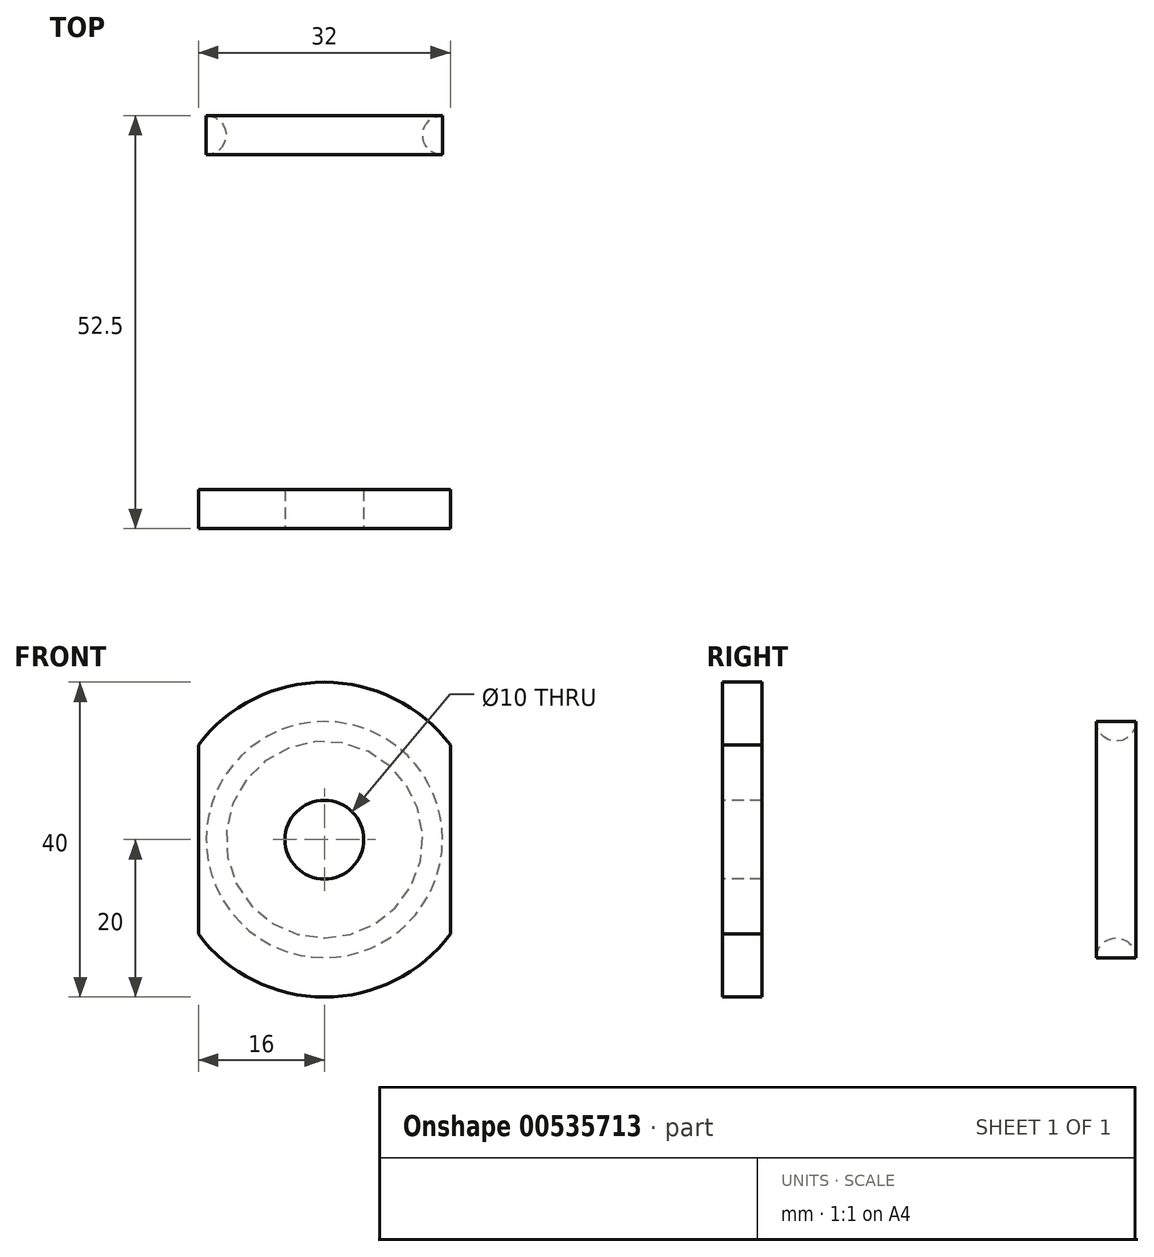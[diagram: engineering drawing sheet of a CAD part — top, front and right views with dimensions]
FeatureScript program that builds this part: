
annotation { "Feature Type Name" : "Feature", "Feature Type Description" : "" }
export const myFeature = defineFeature(function(context is Context, id is Id, definition is map)
    precondition{}
    {
        {
            var Q0;
            Q0=qCreatedBy(makeId("Front.planeOp"),FACE);
            var sketch = newSketch(context, id + "F0", { "sketchPlane" : qUnion([Q0])});
            skCircle(sketch, "E0", {"center": v(0, 0) * mm, "radius": 20 * mm});
            skLineSegment(sketch, "E1", {"start": v(0, 0) * mm, "end": v(16, 0) * mm});
            skLineSegment(sketch, "E2", {"start": v(16, 0) * mm, "end": v(16, 12) * mm});
            skLineSegment(sketch, "E3", {"start": v(16, 12) * mm, "end": v(16, -12) * mm});
            skLineSegment(sketch, "E4", {"start": v(0, 0) * mm, "end": v(-16, 0) * mm});
            skLineSegment(sketch, "E5", {"start": v(-16, 0) * mm, "end": v(-16, 12) * mm});
            skLineSegment(sketch, "E6", {"start": v(-16, 12) * mm, "end": v(-16, -12) * mm});
            skSolve(sketch);
        }
        {
            var Q0;
            {var subQ1=sQuery(id+"F0.wireOp",EDGE,"E1");Q0=makeQuery(id+"F0.imprint","IMPRINT",FACE,{"disambiguationData":[TD([[makeQuery(id+"F0.imprint","IMPRINT",EDGE,{"derivedFrom":subQ1}),1.0]])]});}
            var Q1;
            {var subQ1=sQuery(id+"F0.wireOp",EDGE,"E1");Q1=makeQuery(id+"F0.imprint","IMPRINT",FACE,{"disambiguationData":[TD([[makeQuery(id+"F0.imprint","IMPRINT",EDGE,{"derivedFrom":subQ1}),-1.0]])]});}
            extrude(context, id + "F1", {"entities" : qUnion([Q0, Q1]), "depth" : 5 * mm, "offsetDistance" : 25 * mm});
        }
        {
            var Q0;
            {var subQ1=sQuery(id+"F0.wireOp",EDGE,"E1");Q0=makeQuery(id+"F0.imprint","IMPRINT",FACE,{"disambiguationData":[TD([[makeQuery(id+"F0.imprint","IMPRINT",EDGE,{"derivedFrom":subQ1}),1.0]])]});}
            var sketch = newSketch(context, id + "F2", { "sketchPlane" : qUnion([Q0])});
            skCircle(sketch, "E7", {"center": v(0, 0) * mm, "radius": 15 * mm});
            skSolve(sketch);
        }
        {
            var Q0;
            Q0=qSketchRegion(id+"F2",true);
            extrude(context, id + "F3", {"entities" : qUnion([Q0]), "operationType" : NewBodyOperationType.ADD, "oppositeDirection" : true, "depth" : 55 * mm, "offsetDistance" : 25 * mm});
        }
        {
            var Q0;
            Q0=qCreatedBy(makeId("Front.planeOp"),FACE);
            var sketch = newSketch(context, id + "F4", { "sketchPlane" : qUnion([Q0])});
            skCircle(sketch, "E8", {"center": v(0, 0) * mm, "radius": 5 * mm});
            skSolve(sketch);
        }
        {
            var Q0;
            Q0=qSketchRegion(id+"F4",true);
            extrude(context, id + "F5", {"entities" : qUnion([Q0]), "operationType" : NewBodyOperationType.REMOVE, "endBound" : BoundingType.UP_TO_NEXT, "oppositeDirection" : true, "depth" : 25 * mm, "offsetDistance" : 25 * mm});
        }
        {
            var Q0;
            Q0=qSketchRegion(id+"F4",true);
            extrude(context, id + "F6", {"entities" : qUnion([Q0]), "operationType" : NewBodyOperationType.REMOVE, "endBound" : BoundingType.UP_TO_NEXT, "depth" : 25 * mm, "offsetDistance" : 25 * mm});
        }
        {
            var Q0;
            Q0=qCreatedBy(makeId("Right.planeOp"),FACE);
            var sketch = newSketch(context, id + "F7", { "sketchPlane" : qUnion([Q0])});
            skLineSegment(sketch, "E9.bottom", {"start": v(0, 0) * mm, "end": v(55, 0) * mm});
            skLineSegment(sketch, "E9.top", {"start": v(0, 15) * mm, "end": v(55, 15) * mm});
            skLineSegment(sketch, "E9.left", {"start": v(0, 0) * mm, "end": v(0, 15) * mm});
            skLineSegment(sketch, "E9.right", {"start": v(55, 0) * mm, "end": v(55, 15) * mm});
            skLineSegment(sketch, "E10", {"start": v(55, 15) * mm, "end": v(45, 15) * mm});
            skCircle(sketch, "E11", {"center": v(45, 15) * mm, "radius": 2.5 * mm});
            skLineSegment(sketch, "E12", {"start": v(54, 15) * mm, "end": v(55, 14) * mm});
            skLineSegment(sketch, "E13", {"start": v(54, 15) * mm, "end": v(55, 15) * mm});
            skLineSegment(sketch, "E14", {"start": v(55, 14) * mm, "end": v(55, 15) * mm});
            skSolve(sketch);
        }
        {
            var Q0;
            {var subQ0=sQuery(id+"F7.wireOp",EDGE,"E10");var subQ1=sQuery(id+"F7.wireOp",EDGE,"E9.top");var subQ2=makeQuery(id+"F7.imprint","INTERSECT",VERTEX,{"derivedFrom":[subQ1,subQ0]});Q0=makeQuery(id+"F7.imprint","IMPRINT",FACE,{"disambiguationData":[TD([[makeQuery(id+"F7.imprint","IMPRINT",EDGE,{"disambiguationData":[TD([[subQ2,1.0]])],"derivedFrom":subQ1}),-1.0]])]});}
            var Q1;
            Q1=makeQuery(id+"F3.opExtrude","SWEPT_FACE",FACE,{"disambiguationData":[OSD([sQuery(id+"F2.wireOp",EDGE,"E7")])]});
            revolve(context, id + "F8", {"operationType" : NewBodyOperationType.REMOVE, "entities" : qUnion([Q0]), "axis" : qUnion([Q1]), "revolveType" : RevolveType.FULL, "oppositeDirection" : true});
        }
        {
            var Q0;
            Q0=makeQuery(id+"F7.imprint","IMPRINT",FACE,{"disambiguationData":[TD([[makeQuery(id+"F7.imprint","IMPRINT",EDGE,{"derivedFrom":sQuery(id+"F7.wireOp",EDGE,"E12")}),1.0]])]});
            var Q1;
            {var subQ0=sQuery(id+"F2.wireOp",EDGE,"E7");Q1=makeQuery(id+"F8.boolean.opBoolean","SPLIT",FACE,{"disambiguationData":[TD([makeQuery(id+"F3.opExtrude","CAP_FACE",FACE,{"disambiguationData":[OSD([subQ0])],"isStart":false})])],"derivedFrom":makeQuery(id+"F3.opExtrude","SWEPT_FACE",FACE,{"disambiguationData":[OSD([subQ0])]})});}
            revolve(context, id + "F9", {"operationType" : NewBodyOperationType.REMOVE, "entities" : qUnion([Q0]), "axis" : qUnion([Q1]), "revolveType" : RevolveType.FULL, "oppositeDirection" : true});
        }
    });
